# Revit family: Geräteeinsätze GES_Geräteeinsatz_Revisionsabdeckung ZESR9
name_source: partatom
category: Generic Models
revit_build: Autodesk Revit 2015 (Build: 20140606_1530(x64)
units: mm (PartAtom-declared; Revit-internal decimal feet)

## types (3) — shared parameters
Bodenbelagdicke = 5 mm  [stored 0.0164042 ft]
Diameter dimesion = 304 mm  [stored 0.997375 ft]
Height = 51 mm
Inner cut = 295 mm  [stored 0.967848 ft]
Inner cut2 = 230 mm  [stored 0.754593 ft]
Manufacturer = OBO Bettermann
Outer Diameter Dimension = 324 mm  [stored 1.06299 ft]
URL = http://www.obo-bettermann.com

## per-type parameters (varying)
| type | GTIN | Inner cut 3 | Manufacturer Art. No. | Material |
| ZESR9-2 U12T 7011 | 4012195894063 | 209 mm  [stored 0.685696 ft] | 7406805 | Plastic RAL 7011 |
| ZESR9-2 U12T 9011 | 4012195894094 | 165 mm | 7406806 | Plastic RAL 9011 |
| ZESR9-2 U12T 1019 | 4012195894100 | 209 mm  [stored 0.685696 ft] | 7406807 | Plastic RAL 1019 |

note: column(s) folded — value = type name in every type: Article Type

note: [stored X ft] marks values corroborated as IEEE doubles in the binary element streams (Revit-internal decimal feet)

## geometry (parser evidence)
native form markers: Sweep x2
no freeform markers — native parametric forms only
